# Revit family: Outdoor-Kitchen-Cabinets_Kalamazoo_Storage-Cabinets_Arcadia
name_source: partatom
category: Specialty Equipment
revit_build: Autodesk Revit 2018 (Build: 20190510_1515(x64)
units: mm (PartAtom-declared; Revit-internal decimal feet)

## family parameters
Always vertical = Yes
Cut with Voids When Loaded = No
OmniClass Number = 23.40.40.11
OmniClass Title = Specialized Food Storage and Display Furnishings
Part Type = Normal
Room Calculation Point = No
Round Connector Dimension = Use Diameter
Shared = No
Work Plane-Based = No

## types (16) — shared parameters
Assembly Code = E1090300
Depth = 29 1/8"
Keynote = 11400
Manufacturer = Kalamazoo Outdoor Gourmet
Product Material = Kalamazoo - Stainless Steel - 304 OR 316L
Product data url = https://www.bimobject.com
URL = https://kalamazoogourmet.com
Ι_Gnrc Mdl Optn 01 = Extension : +3/4"
Ι_Gnrc Mdl Optn 02 = Extension : -3/4"

## per-type parameters (varying)
| type | 2 | 3 | DBL | Description | SNGL | Weight (lb) | Width |
| KD-12-1 | No | No | No | Arcadia 12-Inch Pull-Out Rack Storage Cabinet | Yes | 180.00 lbf | 12" |
| KD-12-2 | Yes | No | No | Arcadia 12-Inch Drawer Over Door Storage Cabinet | Yes | 180.00 lbf | 12" |
| KD-12-3 | Yes | Yes | No | Arcadia 12-Inch Three Drawer Storage Cabinet | Yes | 180.00 lbf | 12" |
| KD-15-2 | Yes | No | No | Arcadia 15-Inch Drawer Over Door Storage Cabinet | Yes | 190.00 lbf | 15" |
| KD-15-3 | Yes | Yes | No | Arcadia 15-Inch Three Drawer Storage Cabinet | Yes | 190.00 lbf | 15" |
| KD-18-1 | No | No | No | Arcadia 18-Inch Waste & Recycling Storage Cabinet | Yes | 200.00 lbf | 18" |
| KD-18-2 | Yes | No | No | Arcadia 18-Inch Drawer Over Door Storage Cabinet | Yes | 200.00 lbf | 18" |
| KD-18-3 | Yes | Yes | No | Arcadia 18-Inch Three Drawer Storage Cabinet | Yes | 200.00 lbf | 18" |
| KD-21-1 | No | No | No | Arcadia 21-Inch Waste & Recycling Storage Cabinet | Yes | 210.00 lbf | 21" |
| KD-21-2 | Yes | No | No | Arcadia 21-Inch Drawer Over Door Storage Cabinet | Yes | 210.00 lbf | 21" |
| KD-21-3 | Yes | Yes | No | Arcadia 21-Inch Three Drawer Storage Cabinet | Yes | 210.00 lbf | 21" |
| KD-24-1 | No | No | No | Arcadia 24-Inch Waste & Recycling Storage Cabinet | Yes | 220.00 lbf | 24" |
| KD-24-2 | Yes | No | No | Arcadia 24-Inch Drawer Over Door Storage Cabinet | Yes | 220.00 lbf | 24" |
| KD-24-3 | Yes | Yes | No | Arcadia 24-Inch Three Drawer Storage Cabinet | Yes | 220.00 lbf | 24" |
| KD-30-4 | No | No | Yes | Arcadia 30-Inch Storage Cabinet | No | 240.00 lbf | 30" |
| KD-36-4 | No | No | Yes | Arcadia 36-Inch Storage Cabinet | No | 250.00 lbf | 36" |

note: column(s) folded — value = type name in every type: Model

## geometry (parser evidence)
native form markers: Sweep x6
no freeform markers — native parametric forms only
